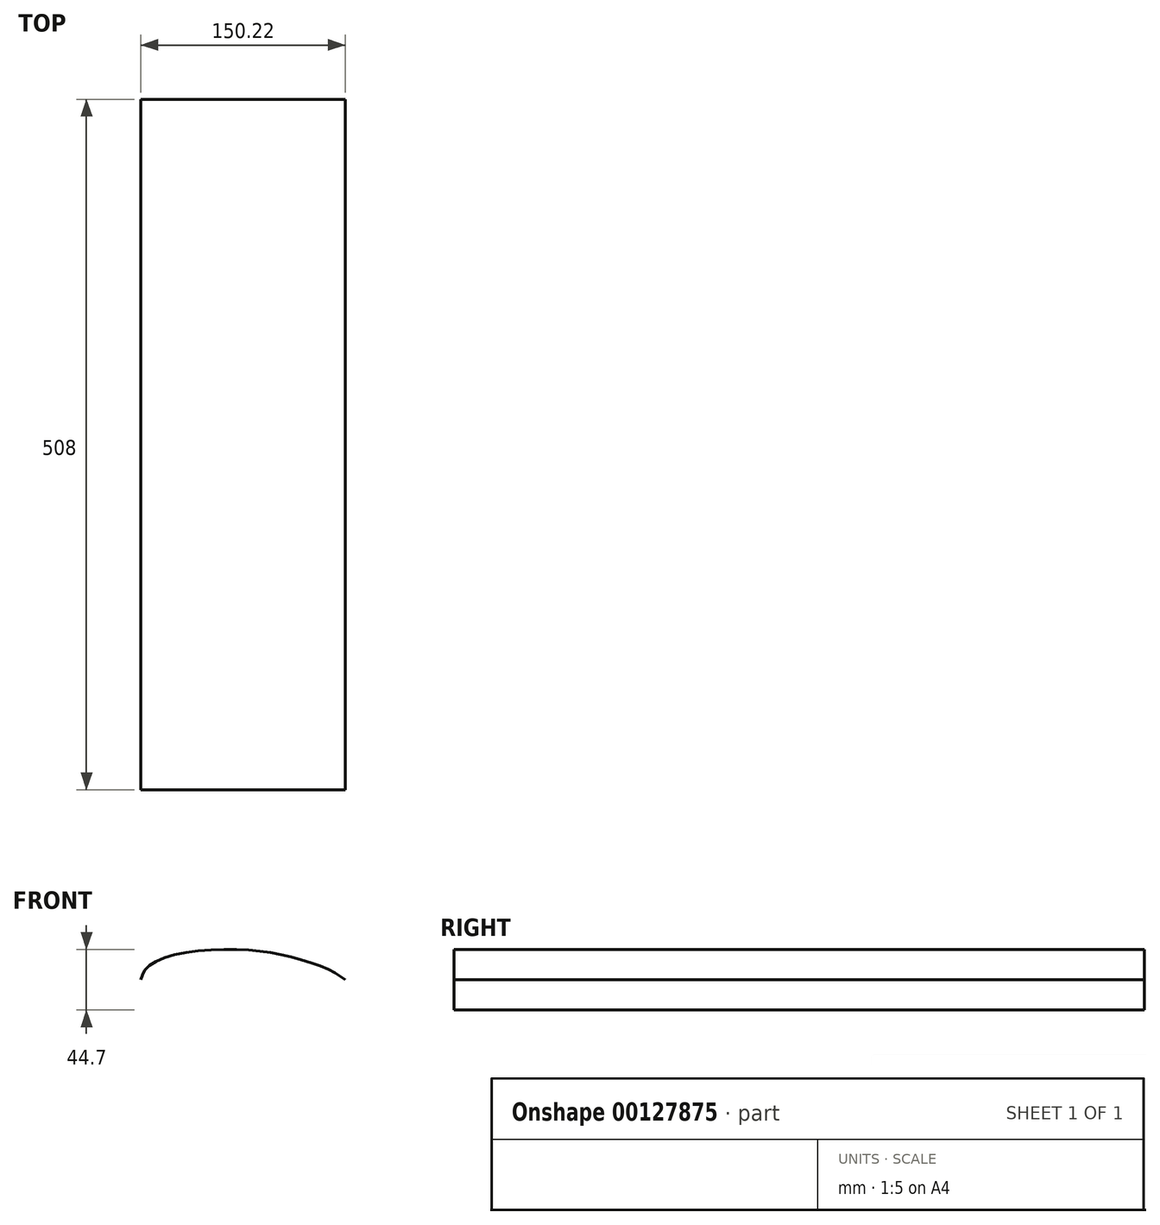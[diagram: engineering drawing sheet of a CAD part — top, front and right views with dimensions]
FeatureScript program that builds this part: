
annotation { "Feature Type Name" : "Feature", "Feature Type Description" : "" }
export const myFeature = defineFeature(function(context is Context, id is Id, definition is map)
    precondition{}
    {
        {
            var Q0;
            Q0=qCreatedBy(makeId("Front.planeOp"),FACE);
            var sketch = newSketch(context, id + "F0", { "sketchPlane" : qUnion([Q0])});
            skFitSpline(sketch, "E0", {"points": [v(0, 0) * mm, v(3.4, 7.82) * mm, v(23.94, 18.19) * mm, v(73.13, 22.15) * mm, v(110.45, 16.68) * mm, v(138.91, 7.07) * mm, v(150.22, 0) * mm], "startDerivative": vector(19.39, 81.89) * mm, "endDerivative": vector(78.07, -58.99) * mm});
            skLineSegment(sketch, "E1", {"start": v(0, 0) * mm, "end": v(150.22, 0) * mm});
            skSolve(sketch);
        }
        {
            var Q0;
            Q0 = qSketchRegion(id + "F0", true);
            extrude(context, id + "F1", {"entities" : qUnion([Q0]), "depth" : 254 * mm, "hasSecondDirection" : true, "secondDirectionOppositeDirection" : true, "secondDirectionDepth" : 254 * mm});
        }
        {
            var Q0;
            Q0=makeQuery(id+"F1.opExtrude","SWEPT_BODY",BODY,{"disambiguationData":[OSD([sQuery(id+"F0.wireOp",EDGE,"E0"),sQuery(id+"F0.wireOp",EDGE,"E1")])]});
            var Q1;
            Q1=makeQuery(id+"F1.opExtrude","SWEPT_FACE",FACE,{"disambiguationData":[OSD([sQuery(id+"F0.wireOp",EDGE,"E1")])]});
            mirror(context, id + "F2", {"operationType" : NewBodyOperationType.ADD, "entities" : qUnion([Q0]), "mirrorPlane" : qUnion([Q1])});
        }
    });
